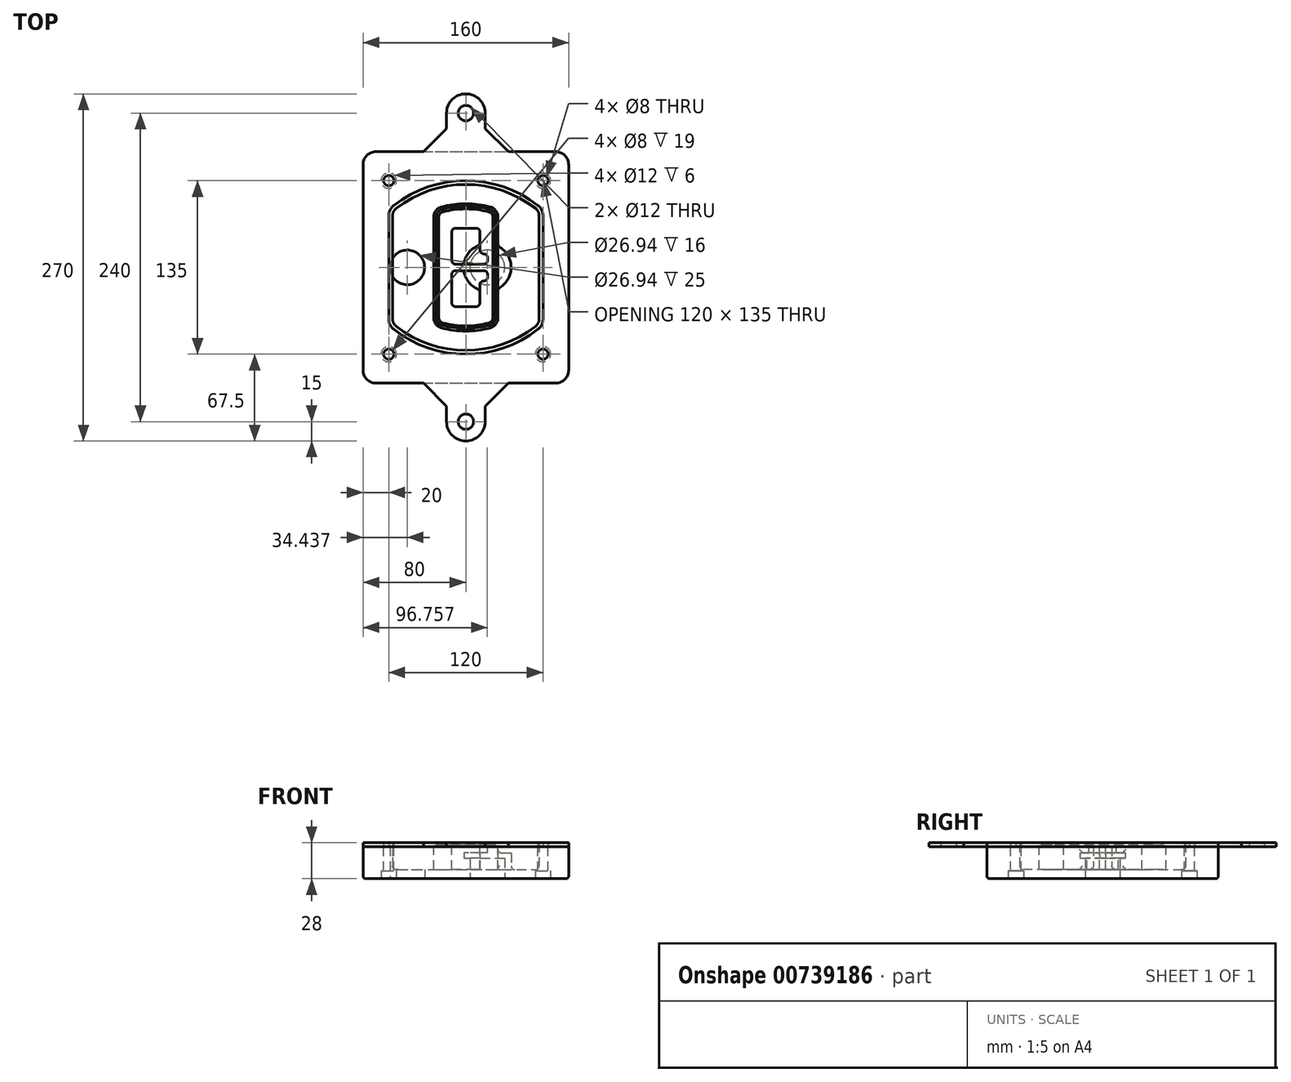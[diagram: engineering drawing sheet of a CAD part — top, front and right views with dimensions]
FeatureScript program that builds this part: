
annotation { "Feature Type Name" : "Feature", "Feature Type Description" : "" }
export const myFeature = defineFeature(function(context is Context, id is Id, definition is map)
    precondition{}
    {
        {
            var Q0;
            Q0=qCreatedBy(makeId("Top.planeOp"),FACE);
            var sketch = newSketch(context, id + "F0", { "sketchPlane" : qUnion([Q0])});
            skPoint(sketch, "E0.rect.middle", {"position": v(0, 0) * mm});
            skLineSegment(sketch, "E1.bottom", {"start": v(-70, -90) * mm, "end": v(70, -90) * mm});
            skLineSegment(sketch, "E1.top", {"start": v(-70, 90) * mm, "end": v(70, 90) * mm});
            skLineSegment(sketch, "E1.left", {"start": v(-80, -80) * mm, "end": v(-80, 80) * mm});
            skLineSegment(sketch, "E1.right", {"start": v(80, -80) * mm, "end": v(80, 80) * mm});
            skLineSegment(sketch, "E2", {"start": v(-80, 90) * mm, "end": v(80, -90) * mm, "construction": true});
            skLineSegment(sketch, "E3", {"start": v(80, 90) * mm, "end": v(-80, -90) * mm, "construction": true});
            skCircle(sketch, "E4", {"center": v(-60, 67.5) * mm, "radius": 4 * mm});
            skCircle(sketch, "E5", {"center": v(60, 67.5) * mm, "radius": 4 * mm});
            skCircle(sketch, "E6", {"center": v(60, -67.5) * mm, "radius": 4 * mm});
            skCircle(sketch, "E7", {"center": v(-60, -67.5) * mm, "radius": 4 * mm});
            skLineSegment(sketch, "E8", {"start": v(-60, 67.5) * mm, "end": v(60, 67.5) * mm, "construction": true});
            skLineSegment(sketch, "E9", {"start": v(60, 67.5) * mm, "end": v(60, -67.5) * mm, "construction": true});
            skLineSegment(sketch, "E10", {"start": v(60, -67.5) * mm, "end": v(-60, -67.5) * mm, "construction": true});
            skLineSegment(sketch, "E11", {"start": v(-60, -67.5) * mm, "end": v(-60, 67.5) * mm, "construction": true});
            skLineSegment(sketch, "E12", {"start": v(-60, 40.3) * mm, "end": v(-60, -40.3) * mm});
            skLineSegment(sketch, "E13", {"start": v(60, 40.3) * mm, "end": v(60, -40.3) * mm});
            skArc(sketch, "E14", {"start": v(56.15, 48.18) * mm, "mid": v(0, 67.5) * mm, "end": v(-56.15, 48.18) * mm});
            skArc(sketch, "E15", {"start": v(-56.15, -48.18) * mm, "mid": v(0, -67.5) * mm, "end": v(56.15, -48.18) * mm});
            skLineSegment(sketch, "E16", {"start": v(-60, 0) * mm, "end": v(60, 0) * mm, "construction": true});
            skPoint(sketch, "E17.visualSharp", {"position": v(-60, -45) * mm});
            skArc(sketch, "E17.filletArc", {"start": v(-60, -40.3) * mm, "mid": v(-58.99, -44.68) * mm, "end": v(-56.15, -48.18) * mm});
            skPoint(sketch, "E18.visualSharp", {"position": v(-60, 45) * mm});
            skArc(sketch, "E18.filletArc", {"start": v(-56.15, 48.18) * mm, "mid": v(-58.99, 44.68) * mm, "end": v(-60, 40.3) * mm});
            skPoint(sketch, "E19.visualSharp", {"position": v(60, 45) * mm});
            skArc(sketch, "E19.filletArc", {"start": v(60, 40.3) * mm, "mid": v(58.99, 44.68) * mm, "end": v(56.15, 48.18) * mm});
            skPoint(sketch, "E20.visualSharp", {"position": v(60, -45) * mm});
            skArc(sketch, "E20.filletArc", {"start": v(56.15, -48.18) * mm, "mid": v(58.99, -44.68) * mm, "end": v(60, -40.3) * mm});
            skPoint(sketch, "E21.visualSharp", {"position": v(-80, 90) * mm});
            skArc(sketch, "E21.filletArc", {"start": v(-70, 90) * mm, "mid": v(-77.07, 87.07) * mm, "end": v(-80, 80) * mm});
            skPoint(sketch, "E22.visualSharp", {"position": v(80, 90) * mm});
            skArc(sketch, "E22.filletArc", {"start": v(80, 80) * mm, "mid": v(77.07, 87.07) * mm, "end": v(70, 90) * mm});
            skPoint(sketch, "E23.visualSharp", {"position": v(80, -90) * mm});
            skArc(sketch, "E23.filletArc", {"start": v(70, -90) * mm, "mid": v(77.07, -87.07) * mm, "end": v(80, -80) * mm});
            skPoint(sketch, "E24.visualSharp", {"position": v(-80, -90) * mm});
            skArc(sketch, "E24.filletArc", {"start": v(-80, -80) * mm, "mid": v(-77.07, -87.07) * mm, "end": v(-70, -90) * mm});
            skArc(sketch, "E25.0", {"start": v(57, 40.3) * mm, "mid": v(56.3, 43.36) * mm, "end": v(54.3, 45.81) * mm});
            skLineSegment(sketch, "E25.1", {"start": v(57, 40.3) * mm, "end": v(57, -40.3) * mm});
            skArc(sketch, "E25.2", {"start": v(54.3, -45.81) * mm, "mid": v(56.3, -43.36) * mm, "end": v(57, -40.3) * mm});
            skArc(sketch, "E25.3", {"start": v(-54.3, -45.81) * mm, "mid": v(0, -64.5) * mm, "end": v(54.3, -45.81) * mm});
            skArc(sketch, "E25.4", {"start": v(-57, -40.3) * mm, "mid": v(-56.3, -43.36) * mm, "end": v(-54.3, -45.81) * mm});
            skArc(sketch, "E25.5", {"start": v(54.3, 45.81) * mm, "mid": v(0, 64.5) * mm, "end": v(-54.3, 45.81) * mm});
            skLineSegment(sketch, "E25.6", {"start": v(-57, 40.3) * mm, "end": v(-57, -40.3) * mm});
            skArc(sketch, "E25.7", {"start": v(-54.3, 45.81) * mm, "mid": v(-56.3, 43.36) * mm, "end": v(-57, 40.3) * mm});
            skArc(sketch, "E26.0", {"start": v(-58.62, 51.33) * mm, "mid": v(-62.58, 46.43) * mm, "end": v(-64, 40.3) * mm});
            skArc(sketch, "E26.1", {"start": v(58.62, 51.33) * mm, "mid": v(0, 71.5) * mm, "end": v(-58.62, 51.33) * mm});
            skArc(sketch, "E26.2", {"start": v(64, 40.3) * mm, "mid": v(62.58, 46.43) * mm, "end": v(58.62, 51.33) * mm});
            skLineSegment(sketch, "E26.3", {"start": v(64, 40.3) * mm, "end": v(64, -40.3) * mm});
            skArc(sketch, "E26.4", {"start": v(58.62, -51.33) * mm, "mid": v(62.58, -46.43) * mm, "end": v(64, -40.3) * mm});
            skLineSegment(sketch, "E26.5", {"start": v(-64, 40.3) * mm, "end": v(-64, -40.3) * mm});
            skArc(sketch, "E26.6", {"start": v(-58.62, -51.33) * mm, "mid": v(0, -71.5) * mm, "end": v(58.62, -51.33) * mm});
            skArc(sketch, "E26.7", {"start": v(-64, -40.3) * mm, "mid": v(-62.58, -46.43) * mm, "end": v(-58.62, -51.33) * mm});
            skSolve(sketch);
        }
        {
            var Q0;
            Q0=makeQuery(id+"F0.imprint","IMPRINT",FACE,{"disambiguationData":[TD([[makeQuery(id+"F0.imprint","IMPRINT",EDGE,{"derivedFrom":sQuery(id+"F0.wireOp",EDGE,"E1.bottom")}),1.0]])]});
            var Q1;
            Q1=makeQuery(id+"F0.imprint","IMPRINT",FACE,{"disambiguationData":[TD([[makeQuery(id+"F0.imprint","IMPRINT",EDGE,{"derivedFrom":sQuery(id+"F0.wireOp",EDGE,"E12")}),1.0]])]});
            var Q2;
            Q2=makeQuery(id+"F0.imprint","IMPRINT",FACE,{"disambiguationData":[TD([[makeQuery(id+"F0.imprint","IMPRINT",EDGE,{"derivedFrom":sQuery(id+"F0.wireOp",EDGE,"E25.0")}),1.0]])]});
            var Q3;
            Q3=makeQuery(id+"F0.imprint","IMPRINT",FACE,{"disambiguationData":[TD([[makeQuery(id+"F0.imprint","IMPRINT",EDGE,{"derivedFrom":sQuery(id+"F0.wireOp",EDGE,"E12")}),-1.0]])]});
            extrude(context, id + "F1", {"entities" : qUnion([Q0, Q1, Q2, Q3]), "oppositeDirection" : true, "depth" : 25 * mm});
        }
        {
            var Q0;
            Q0=makeQuery(id+"F0.imprint","IMPRINT",FACE,{"disambiguationData":[TD([[makeQuery(id+"F0.imprint","IMPRINT",EDGE,{"derivedFrom":sQuery(id+"F0.wireOp",EDGE,"E12")}),1.0]])]});
            extrude(context, id + "F2", {"entities" : qUnion([Q0]), "operationType" : NewBodyOperationType.ADD, "depth" : 3 * mm});
        }
        {
            var Q0;
            Q0=makeQuery(id+"F0.imprint","IMPRINT",FACE,{"disambiguationData":[TD([[makeQuery(id+"F0.imprint","IMPRINT",EDGE,{"derivedFrom":sQuery(id+"F0.wireOp",EDGE,"E25.0")}),1.0]])]});
            extrude(context, id + "F3", {"entities" : qUnion([Q0]), "operationType" : NewBodyOperationType.REMOVE, "oppositeDirection" : true, "depth" : 18 * mm});
        }
        {
            var Q0;
            Q0=makeQuery(id+"F2.opExtrude","CAP_FACE",FACE,{"disambiguationData":[OSD([sQuery(id+"F0.wireOp",EDGE,"E12"),sQuery(id+"F0.wireOp",EDGE,"E13"),sQuery(id+"F0.wireOp",EDGE,"E14"),sQuery(id+"F0.wireOp",EDGE,"E15"),sQuery(id+"F0.wireOp",EDGE,"E17.filletArc"),sQuery(id+"F0.wireOp",EDGE,"E18.filletArc"),sQuery(id+"F0.wireOp",EDGE,"E19.filletArc"),sQuery(id+"F0.wireOp",EDGE,"E20.filletArc"),sQuery(id+"F0.wireOp",EDGE,"E25.0"),sQuery(id+"F0.wireOp",EDGE,"E25.1"),sQuery(id+"F0.wireOp",EDGE,"E25.2"),sQuery(id+"F0.wireOp",EDGE,"E25.3"),sQuery(id+"F0.wireOp",EDGE,"E25.4"),sQuery(id+"F0.wireOp",EDGE,"E25.5"),sQuery(id+"F0.wireOp",EDGE,"E25.6"),sQuery(id+"F0.wireOp",EDGE,"E25.7")])],"isStart":false});
            var sketch = newSketch(context, id + "F4", { "sketchPlane" : qUnion([Q0])});
            skArc(sketch, "E27.0", {"start": v(-19.08, -46.97) * mm, "mid": v(0, -49.5) * mm, "end": v(19.08, -46.97) * mm});
            skArc(sketch, "E28.0", {"start": v(19.08, 46.97) * mm, "mid": v(0, 49.5) * mm, "end": v(-19.08, 46.97) * mm});
            skLineSegment(sketch, "E29", {"start": v(-25, 39.25) * mm, "end": v(-25, -39.25) * mm});
            skLineSegment(sketch, "E30", {"start": v(25, 39.25) * mm, "end": v(25, -39.25) * mm});
            skLineSegment(sketch, "E31", {"start": v(-25, 45.1) * mm, "end": v(25, 45.1) * mm, "construction": true});
            skLineSegment(sketch, "E32", {"start": v(-25, -45.1) * mm, "end": v(25, -45.1) * mm, "construction": true});
            skPoint(sketch, "E33.visualSharp", {"position": v(-25, 45.1) * mm});
            skArc(sketch, "E33.filletArc", {"start": v(-19.08, 46.97) * mm, "mid": v(-23.35, 44.11) * mm, "end": v(-25, 39.25) * mm});
            skPoint(sketch, "E34.visualSharp", {"position": v(25, 45.1) * mm});
            skArc(sketch, "E34.filletArc", {"start": v(25, 39.25) * mm, "mid": v(23.35, 44.11) * mm, "end": v(19.08, 46.97) * mm});
            skPoint(sketch, "E35.visualSharp", {"position": v(25, -45.1) * mm});
            skArc(sketch, "E35.filletArc", {"start": v(19.08, -46.97) * mm, "mid": v(23.35, -44.11) * mm, "end": v(25, -39.25) * mm});
            skPoint(sketch, "E36.visualSharp", {"position": v(-25, -45.1) * mm});
            skArc(sketch, "E36.filletArc", {"start": v(-25, -39.25) * mm, "mid": v(-23.35, -44.11) * mm, "end": v(-19.08, -46.97) * mm});
            skArc(sketch, "E37.0", {"start": v(54.3, 45.81) * mm, "mid": v(0, 64.5) * mm, "end": v(-54.3, 45.81) * mm});
            skArc(sketch, "E37.1", {"start": v(-54.3, 45.81) * mm, "mid": v(-56.3, 43.36) * mm, "end": v(-57, 40.3) * mm});
            skLineSegment(sketch, "E37.2", {"start": v(-57, 40.3) * mm, "end": v(-57, -40.3) * mm});
            skArc(sketch, "E37.3", {"start": v(-57, -40.3) * mm, "mid": v(-56.3, -43.36) * mm, "end": v(-54.3, -45.81) * mm});
            skArc(sketch, "E37.4", {"start": v(-54.3, -45.81) * mm, "mid": v(0, -64.5) * mm, "end": v(54.3, -45.81) * mm});
            skArc(sketch, "E37.5", {"start": v(54.3, -45.81) * mm, "mid": v(56.3, -43.36) * mm, "end": v(57, -40.3) * mm});
            skLineSegment(sketch, "E37.6", {"start": v(57, 40.3) * mm, "end": v(57, -40.3) * mm});
            skArc(sketch, "E37.7", {"start": v(57, 40.3) * mm, "mid": v(56.3, 43.36) * mm, "end": v(54.3, 45.81) * mm});
            skLineSegment(sketch, "E38.0", {"start": v(23, 39.25) * mm, "end": v(23, -39.25) * mm});
            skArc(sketch, "E38.1", {"start": v(18.56, -45.04) * mm, "mid": v(21.76, -42.9) * mm, "end": v(23, -39.25) * mm});
            skArc(sketch, "E38.2", {"start": v(-18.56, -45.04) * mm, "mid": v(0, -47.5) * mm, "end": v(18.56, -45.04) * mm});
            skArc(sketch, "E38.3", {"start": v(-23, -39.25) * mm, "mid": v(-21.76, -42.9) * mm, "end": v(-18.56, -45.04) * mm});
            skLineSegment(sketch, "E38.4", {"start": v(-23, 39.25) * mm, "end": v(-23, -39.25) * mm});
            skArc(sketch, "E38.5", {"start": v(23, 39.25) * mm, "mid": v(21.76, 42.9) * mm, "end": v(18.56, 45.04) * mm});
            skArc(sketch, "E38.6", {"start": v(-18.56, 45.04) * mm, "mid": v(-21.76, 42.9) * mm, "end": v(-23, 39.25) * mm});
            skArc(sketch, "E38.7", {"start": v(18.56, 45.04) * mm, "mid": v(0, 47.5) * mm, "end": v(-18.56, 45.04) * mm});
            skArc(sketch, "E39.0", {"start": v(21, 39.25) * mm, "mid": v(20.18, 41.68) * mm, "end": v(18.04, 43.1) * mm});
            skLineSegment(sketch, "E39.1", {"start": v(21, 39.25) * mm, "end": v(21, -39.25) * mm});
            skArc(sketch, "E39.2", {"start": v(18.04, -43.1) * mm, "mid": v(20.18, -41.68) * mm, "end": v(21, -39.25) * mm});
            skArc(sketch, "E39.3", {"start": v(-18.04, -43.1) * mm, "mid": v(0, -45.5) * mm, "end": v(18.04, -43.1) * mm});
            skArc(sketch, "E39.4", {"start": v(-21, -39.25) * mm, "mid": v(-20.18, -41.68) * mm, "end": v(-18.04, -43.1) * mm});
            skArc(sketch, "E39.5", {"start": v(18.04, 43.1) * mm, "mid": v(0, 45.5) * mm, "end": v(-18.04, 43.1) * mm});
            skLineSegment(sketch, "E39.6", {"start": v(-21, 39.25) * mm, "end": v(-21, -39.25) * mm});
            skArc(sketch, "E39.7", {"start": v(-18.04, 43.1) * mm, "mid": v(-20.18, 41.68) * mm, "end": v(-21, 39.25) * mm});
            skLineSegment(sketch, "E40", {"start": v(-25, 0) * mm, "end": v(25, 0) * mm, "construction": true});
            skLineSegment(sketch, "E41", {"start": v(-11, 5.5) * mm, "end": v(-11, 27.5) * mm});
            skLineSegment(sketch, "E42", {"start": v(-8, 30.5) * mm, "end": v(8, 30.5) * mm});
            skLineSegment(sketch, "E43", {"start": v(11, 27.5) * mm, "end": v(11, 13.5) * mm});
            skLineSegment(sketch, "E44", {"start": v(14, 10.5) * mm, "end": v(14, 10.5) * mm});
            skLineSegment(sketch, "E45", {"start": v(17, 7.5) * mm, "end": v(17, 5.5) * mm});
            skLineSegment(sketch, "E46", {"start": v(14, 2.5) * mm, "end": v(-8, 2.5) * mm});
            skPoint(sketch, "E47.visualSharp", {"position": v(-11, 30.5) * mm});
            skArc(sketch, "E47.filletArc", {"start": v(-8, 30.5) * mm, "mid": v(-10.12, 29.62) * mm, "end": v(-11, 27.5) * mm});
            skPoint(sketch, "E48.visualSharp", {"position": v(11, 30.5) * mm});
            skArc(sketch, "E48.filletArc", {"start": v(11, 27.5) * mm, "mid": v(10.12, 29.62) * mm, "end": v(8, 30.5) * mm});
            skPoint(sketch, "E49.visualSharp", {"position": v(11, 10.5) * mm});
            skArc(sketch, "E49.filletArc", {"start": v(11, 13.5) * mm, "mid": v(11.88, 11.38) * mm, "end": v(14, 10.5) * mm});
            skPoint(sketch, "E50.visualSharp", {"position": v(17, 10.5) * mm});
            skArc(sketch, "E50.filletArc", {"start": v(17, 7.5) * mm, "mid": v(16.12, 9.62) * mm, "end": v(14, 10.5) * mm});
            skPoint(sketch, "E51.visualSharp", {"position": v(17, 2.5) * mm});
            skArc(sketch, "E51.filletArc", {"start": v(14, 2.5) * mm, "mid": v(16.12, 3.38) * mm, "end": v(17, 5.5) * mm});
            skPoint(sketch, "E52.visualSharp", {"position": v(-11, 2.5) * mm});
            skArc(sketch, "E52.filletArc", {"start": v(-11, 5.5) * mm, "mid": v(-10.12, 3.38) * mm, "end": v(-8, 2.5) * mm});
            skLineSegment(sketch, "E53.0.MirrorCS", {"start": v(14, -2.5) * mm, "end": v(-8, -2.5) * mm});
            skArc(sketch, "E54.0.MirrorCS", {"start": v(-11, -5.5) * mm, "mid": v(-10.12, -3.38) * mm, "end": v(-8, -2.5) * mm});
            skLineSegment(sketch, "E55.0.MirrorCS", {"start": v(-11, -5.5) * mm, "end": v(-11, -27.5) * mm});
            skArc(sketch, "E56.0.MirrorCS", {"start": v(-8, -30.5) * mm, "mid": v(-10.12, -29.62) * mm, "end": v(-11, -27.5) * mm});
            skLineSegment(sketch, "E57.0.MirrorCS", {"start": v(-8, -30.5) * mm, "end": v(8, -30.5) * mm});
            skArc(sketch, "E58.0.MirrorCS", {"start": v(11, -27.5) * mm, "mid": v(10.12, -29.62) * mm, "end": v(8, -30.5) * mm});
            skLineSegment(sketch, "E59.0.MirrorCS", {"start": v(11, -27.5) * mm, "end": v(11, -13.5) * mm});
            skArc(sketch, "E60.0.MirrorCS", {"start": v(11, -13.5) * mm, "mid": v(11.88, -11.38) * mm, "end": v(14, -10.5) * mm});
            skArc(sketch, "E61.0.MirrorCS", {"start": v(17, -7.5) * mm, "mid": v(16.12, -9.62) * mm, "end": v(14, -10.5) * mm});
            skLineSegment(sketch, "E62.0.MirrorCS", {"start": v(17, -7.5) * mm, "end": v(17, -5.5) * mm});
            skArc(sketch, "E63.0.MirrorCS", {"start": v(14, -2.5) * mm, "mid": v(16.12, -3.38) * mm, "end": v(17, -5.5) * mm});
            skSolve(sketch);
        }
        {
            var Q0;
            Q0=makeQuery(id+"F4.imprint","IMPRINT",FACE,{"disambiguationData":[TD([[makeQuery(id+"F4.imprint","IMPRINT",EDGE,{"derivedFrom":sQuery(id+"F4.wireOp",EDGE,"E27.0")}),1.0]])]});
            var Q1;
            Q1=makeQuery(id+"F4.imprint","IMPRINT",FACE,{"disambiguationData":[TD([[makeQuery(id+"F4.imprint","IMPRINT",EDGE,{"derivedFrom":sQuery(id+"F4.wireOp",EDGE,"E38.0")}),-1.0]])]});
            var Q2;
            Q2=makeQuery(id+"F4.imprint","IMPRINT",FACE,{"disambiguationData":[TD([[makeQuery(id+"F4.imprint","IMPRINT",EDGE,{"derivedFrom":sQuery(id+"F4.wireOp",EDGE,"E39.0")}),1.0]])]});
            extrude(context, id + "F5", {"entities" : qUnion([Q0, Q1, Q2]), "operationType" : NewBodyOperationType.ADD, "endBound" : BoundingType.UP_TO_NEXT, "oppositeDirection" : true, "depth" : 25 * mm});
        }
        {
            var Q0;
            Q0=makeQuery(id+"F4.imprint","IMPRINT",FACE,{"disambiguationData":[TD([[makeQuery(id+"F4.imprint","IMPRINT",EDGE,{"derivedFrom":sQuery(id+"F4.wireOp",EDGE,"E38.0")}),-1.0]])]});
            extrude(context, id + "F6", {"entities" : qUnion([Q0]), "operationType" : NewBodyOperationType.REMOVE, "oppositeDirection" : true, "depth" : 2 * mm});
        }
        {
            var Q0;
            Q0=makeQuery(id+"F1.opExtrude","CAP_FACE",FACE,{"disambiguationData":[OSD([sQuery(id+"F0.wireOp",EDGE,"E1.bottom"),sQuery(id+"F0.wireOp",EDGE,"E1.top"),sQuery(id+"F0.wireOp",EDGE,"E1.left"),sQuery(id+"F0.wireOp",EDGE,"E1.right"),sQuery(id+"F0.wireOp",EDGE,"E4"),sQuery(id+"F0.wireOp",EDGE,"E5"),sQuery(id+"F0.wireOp",EDGE,"E6"),sQuery(id+"F0.wireOp",EDGE,"E7"),sQuery(id+"F0.wireOp",EDGE,"E21.filletArc"),sQuery(id+"F0.wireOp",EDGE,"E22.filletArc"),sQuery(id+"F0.wireOp",EDGE,"E23.filletArc"),sQuery(id+"F0.wireOp",EDGE,"E24.filletArc")])],"isStart":false});
            var sketch = newSketch(context, id + "F7", { "sketchPlane" : qUnion([Q0])});
            skCircle(sketch, "E64", {"center": v(16.76, 0) * mm, "radius": 13.47 * mm});
            skCircle(sketch, "E65", {"center": v(-45.56, 0) * mm, "radius": 13.47 * mm});
            skLineSegment(sketch, "E66", {"start": v(80, 0) * mm, "end": v(-80, 0) * mm});
            skCircle(sketch, "E67", {"center": v(16.76, 0) * mm, "radius": 18.47 * mm});
            skCircle(sketch, "E68", {"center": v(60, -67.5) * mm, "radius": 6 * mm});
            skCircle(sketch, "E69", {"center": v(-60, -67.5) * mm, "radius": 6 * mm});
            skCircle(sketch, "E70", {"center": v(-60, 67.5) * mm, "radius": 6 * mm});
            skCircle(sketch, "E71", {"center": v(60, 67.5) * mm, "radius": 6 * mm});
            skSolve(sketch);
        }
        {
            var Q0;
            {var subQ1=sQuery(id+"F7.wireOp",EDGE,"E66");var subQ4=sQuery(id+"F7.wireOp",EDGE,"E64");var subQ6=makeQuery(id+"F7.imprint","INTERSECT",VERTEX,{"disambiguationData":[OD(0.0)],"derivedFrom":[subQ4,subQ1]});Q0=makeQuery(id+"F7.imprint","IMPRINT",FACE,{"disambiguationData":[TD([[makeQuery(id+"F7.imprint","IMPRINT",EDGE,{"disambiguationData":[TD([[subQ6,-1.0]])],"derivedFrom":subQ4}),-1.0]])]});}
            var Q1;
            {var subQ0=sQuery(id+"F7.wireOp",EDGE,"E66");var subQ1=sQuery(id+"F7.wireOp",EDGE,"E64");var subQ3=makeQuery(id+"F7.imprint","INTERSECT",VERTEX,{"disambiguationData":[OD(0.0)],"derivedFrom":[subQ1,subQ0]});Q1=makeQuery(id+"F7.imprint","IMPRINT",FACE,{"disambiguationData":[TD([[makeQuery(id+"F7.imprint","IMPRINT",EDGE,{"disambiguationData":[TD([[subQ3,-1.0]])],"derivedFrom":subQ1}),1.0]])]});}
            var Q2;
            {var subQ0=sQuery(id+"F7.wireOp",EDGE,"E66");var subQ1=sQuery(id+"F7.wireOp",EDGE,"E64");var subQ3=makeQuery(id+"F7.imprint","INTERSECT",VERTEX,{"disambiguationData":[OD(0.0)],"derivedFrom":[subQ1,subQ0]});Q2=makeQuery(id+"F7.imprint","IMPRINT",FACE,{"disambiguationData":[TD([[makeQuery(id+"F7.imprint","IMPRINT",EDGE,{"disambiguationData":[TD([[subQ3,1.0]])],"derivedFrom":subQ1}),1.0]])]});}
            var Q3;
            {var subQ1=sQuery(id+"F7.wireOp",EDGE,"E66");var subQ4=sQuery(id+"F7.wireOp",EDGE,"E64");var subQ6=makeQuery(id+"F7.imprint","INTERSECT",VERTEX,{"disambiguationData":[OD(0.0)],"derivedFrom":[subQ4,subQ1]});Q3=makeQuery(id+"F7.imprint","IMPRINT",FACE,{"disambiguationData":[TD([[makeQuery(id+"F7.imprint","IMPRINT",EDGE,{"disambiguationData":[TD([[subQ6,1.0]])],"derivedFrom":subQ4}),-1.0]])]});}
            extrude(context, id + "F8", {"entities" : qUnion([Q0, Q1, Q2, Q3]), "operationType" : NewBodyOperationType.ADD, "oppositeDirection" : true, "depth" : 20 * mm});
        }
        {
            var Q0;
            {var subQ0=sQuery(id+"F7.wireOp",EDGE,"E66");var subQ1=sQuery(id+"F7.wireOp",EDGE,"E64");var subQ3=makeQuery(id+"F7.imprint","INTERSECT",VERTEX,{"disambiguationData":[OD(0.0)],"derivedFrom":[subQ1,subQ0]});Q0=makeQuery(id+"F7.imprint","IMPRINT",FACE,{"disambiguationData":[TD([[makeQuery(id+"F7.imprint","IMPRINT",EDGE,{"disambiguationData":[TD([[subQ3,-1.0]])],"derivedFrom":subQ1}),1.0]])]});}
            var Q1;
            {var subQ0=sQuery(id+"F7.wireOp",EDGE,"E66");var subQ1=sQuery(id+"F7.wireOp",EDGE,"E64");var subQ3=makeQuery(id+"F7.imprint","INTERSECT",VERTEX,{"disambiguationData":[OD(0.0)],"derivedFrom":[subQ1,subQ0]});Q1=makeQuery(id+"F7.imprint","IMPRINT",FACE,{"disambiguationData":[TD([[makeQuery(id+"F7.imprint","IMPRINT",EDGE,{"disambiguationData":[TD([[subQ3,1.0]])],"derivedFrom":subQ1}),1.0]])]});}
            extrude(context, id + "F9", {"entities" : qUnion([Q0, Q1]), "operationType" : NewBodyOperationType.REMOVE, "oppositeDirection" : true, "depth" : 16 * mm});
        }
        {
            var Q0;
            {var subQ0=sQuery(id+"F7.wireOp",EDGE,"E66");var subQ1=sQuery(id+"F7.wireOp",EDGE,"E65");var subQ3=makeQuery(id+"F7.imprint","INTERSECT",VERTEX,{"disambiguationData":[OD(0.0)],"derivedFrom":[subQ1,subQ0]});Q0=makeQuery(id+"F7.imprint","IMPRINT",FACE,{"disambiguationData":[TD([[makeQuery(id+"F7.imprint","IMPRINT",EDGE,{"disambiguationData":[TD([[subQ3,-1.0]])],"derivedFrom":subQ1}),1.0]])]});}
            var Q1;
            {var subQ0=sQuery(id+"F7.wireOp",EDGE,"E66");var subQ1=sQuery(id+"F7.wireOp",EDGE,"E65");var subQ3=makeQuery(id+"F7.imprint","INTERSECT",VERTEX,{"disambiguationData":[OD(0.0)],"derivedFrom":[subQ1,subQ0]});Q1=makeQuery(id+"F7.imprint","IMPRINT",FACE,{"disambiguationData":[TD([[makeQuery(id+"F7.imprint","IMPRINT",EDGE,{"disambiguationData":[TD([[subQ3,1.0]])],"derivedFrom":subQ1}),1.0]])]});}
            extrude(context, id + "F10", {"entities" : qUnion([Q0, Q1]), "operationType" : NewBodyOperationType.REMOVE, "oppositeDirection" : true, "depth" : 25 * mm});
        }
        {
            var Q0;
            Q0=makeQuery(id+"F7.imprint","IMPRINT",FACE,{"disambiguationData":[TD([[makeQuery(id+"F7.imprint","IMPRINT",EDGE,{"derivedFrom":sQuery(id+"F7.wireOp",EDGE,"E68")}),1.0]])]});
            var Q1;
            Q1=makeQuery(id+"F7.imprint","IMPRINT",FACE,{"disambiguationData":[TD([[makeQuery(id+"F7.imprint","IMPRINT",EDGE,{"derivedFrom":makeQuery(id+"F1.opExtrude","CAP_EDGE",EDGE,{"disambiguationData":[OSD([sQuery(id+"F0.wireOp",EDGE,"E5")])],"isStart":false})}),-1.0]])]});
            var Q2;
            Q2=makeQuery(id+"F7.imprint","IMPRINT",FACE,{"disambiguationData":[TD([[makeQuery(id+"F7.imprint","IMPRINT",EDGE,{"derivedFrom":sQuery(id+"F7.wireOp",EDGE,"E69")}),1.0]])]});
            var Q3;
            Q3=makeQuery(id+"F7.imprint","IMPRINT",FACE,{"disambiguationData":[TD([[makeQuery(id+"F7.imprint","IMPRINT",EDGE,{"derivedFrom":makeQuery(id+"F1.opExtrude","CAP_EDGE",EDGE,{"disambiguationData":[OSD([sQuery(id+"F0.wireOp",EDGE,"E4")])],"isStart":false})}),-1.0]])]});
            var Q4;
            Q4=makeQuery(id+"F7.imprint","IMPRINT",FACE,{"disambiguationData":[TD([[makeQuery(id+"F7.imprint","IMPRINT",EDGE,{"derivedFrom":sQuery(id+"F7.wireOp",EDGE,"E70")}),1.0]])]});
            var Q5;
            Q5=makeQuery(id+"F7.imprint","IMPRINT",FACE,{"disambiguationData":[TD([[makeQuery(id+"F7.imprint","IMPRINT",EDGE,{"derivedFrom":makeQuery(id+"F1.opExtrude","CAP_EDGE",EDGE,{"disambiguationData":[OSD([sQuery(id+"F0.wireOp",EDGE,"E7")])],"isStart":false})}),-1.0]])]});
            var Q6;
            Q6=makeQuery(id+"F7.imprint","IMPRINT",FACE,{"disambiguationData":[TD([[makeQuery(id+"F7.imprint","IMPRINT",EDGE,{"derivedFrom":sQuery(id+"F7.wireOp",EDGE,"E71")}),1.0]])]});
            var Q7;
            Q7=makeQuery(id+"F7.imprint","IMPRINT",FACE,{"disambiguationData":[TD([[makeQuery(id+"F7.imprint","IMPRINT",EDGE,{"derivedFrom":makeQuery(id+"F1.opExtrude","CAP_EDGE",EDGE,{"disambiguationData":[OSD([sQuery(id+"F0.wireOp",EDGE,"E6")])],"isStart":false})}),-1.0]])]});
            extrude(context, id + "F11", {"entities" : qUnion([Q0, Q1, Q2, Q3, Q4, Q5, Q6, Q7]), "operationType" : NewBodyOperationType.REMOVE, "oppositeDirection" : true, "depth" : 6 * mm});
        }
        {
            var Q0;
            Q0=makeQuery(id+"F9.boolean.opBoolean","COPY",FACE,{"derivedFrom":makeQuery(id+"F9.opExtrude","CAP_FACE",FACE,{"disambiguationData":[OSD([sQuery(id+"F7.wireOp",EDGE,"E64")])],"isStart":false})});
            var sketch = newSketch(context, id + "F12", { "sketchPlane" : qUnion([Q0])});
            skArc(sketch, "E72.0", {"start": v(11, 17.55) * mm, "mid": v(2.57, 11.82) * mm, "end": v(-1.54, 2.5) * mm});
            skArc(sketch, "E72.1", {"start": v(-1.54, -2.5) * mm, "mid": v(2.57, -11.82) * mm, "end": v(11, -17.55) * mm});
            skLineSegment(sketch, "E73", {"start": v(-1.54, -2.5) * mm, "end": v(14, -2.5) * mm});
            skLineSegment(sketch, "E74.0", {"start": v(14, 2.5) * mm, "end": v(-1.54, 2.5) * mm});
            skArc(sketch, "E74.1", {"start": v(14, 2.5) * mm, "mid": v(16.12, 3.38) * mm, "end": v(17, 5.5) * mm});
            skLineSegment(sketch, "E74.2", {"start": v(17, 7.5) * mm, "end": v(17, 5.5) * mm});
            skArc(sketch, "E74.3", {"start": v(17, 7.5) * mm, "mid": v(16.12, 9.62) * mm, "end": v(14, 10.5) * mm});
            skArc(sketch, "E74.4", {"start": v(11, 13.5) * mm, "mid": v(11.88, 11.38) * mm, "end": v(14, 10.5) * mm});
            skLineSegment(sketch, "E74.5", {"start": v(11, 17.55) * mm, "end": v(11, 13.5) * mm});
            skLineSegment(sketch, "E74.7", {"start": v(14, -2.5) * mm, "end": v(-1.54, -2.5) * mm});
            skArc(sketch, "E74.8", {"start": v(14, -2.5) * mm, "mid": v(16.12, -3.38) * mm, "end": v(17, -5.5) * mm});
            skLineSegment(sketch, "E74.9", {"start": v(17, -7.5) * mm, "end": v(17, -5.5) * mm});
            skArc(sketch, "E74.10", {"start": v(17, -7.5) * mm, "mid": v(16.12, -9.62) * mm, "end": v(14, -10.5) * mm});
            skArc(sketch, "E74.11", {"start": v(11, -13.5) * mm, "mid": v(11.88, -11.38) * mm, "end": v(14, -10.5) * mm});
            skLineSegment(sketch, "E74.12", {"start": v(11, -17.55) * mm, "end": v(11, -13.5) * mm});
            skPoint(sketch, "E75.orphan", {"position": v(11, -27.5) * mm});
            skPoint(sketch, "E76.orphan", {"position": v(-8, -2.5) * mm});
            skPoint(sketch, "E77.orphan", {"position": v(-8, 2.5) * mm});
            skPoint(sketch, "E78.orphan", {"position": v(11, 27.5) * mm});
            skSolve(sketch);
        }
        {
            var Q0;
            {var subQ7=sQuery(id+"F12.wireOp",EDGE,"E72.0");var subQ14=sQuery(id+"F12.wireOp",EDGE,"E72.1");var subQ16=sQuery(id+"F12.wireOp",EDGE,"E74.1");var subQ18=sQuery(id+"F12.wireOp",EDGE,"E74.8");Q0=qUnion([makeQuery(id+"F12.imprint","IMPRINT",FACE,{"disambiguationData":[TD([[makeQuery(id+"F12.imprint","IMPRINT",EDGE,{"derivedFrom":subQ7}),1.0]])]}),makeQuery(id+"F12.imprint","IMPRINT",FACE,{"disambiguationData":[TD([[makeQuery(id+"F12.imprint","IMPRINT",EDGE,{"derivedFrom":subQ14}),1.0]])]}),makeQuery(id+"F12.imprint","IMPRINT",FACE,{"disambiguationData":[TD([[makeQuery(id+"F12.imprint","IMPRINT",EDGE,{"derivedFrom":subQ16}),1.0]])]}),makeQuery(id+"F12.imprint","IMPRINT",FACE,{"disambiguationData":[TD([[makeQuery(id+"F12.imprint","IMPRINT",EDGE,{"derivedFrom":subQ18}),-1.0]])]})]);}
            var Q1;
            Q1=makeQuery(id+"F5.boolean.opBoolean","SPLIT",FACE,{"disambiguationData":[TD([makeQuery(id+"F5.opExtrude","SWEPT_FACE",FACE,{"disambiguationData":[OSD([sQuery(id+"F4.wireOp",EDGE,"E41")])]})])],"derivedFrom":makeQuery(id+"F3.boolean.opBoolean","COPY",FACE,{"derivedFrom":makeQuery(id+"F3.opExtrude","CAP_FACE",FACE,{"disambiguationData":[OSD([sQuery(id+"F0.wireOp",EDGE,"E25.0"),sQuery(id+"F0.wireOp",EDGE,"E25.1"),sQuery(id+"F0.wireOp",EDGE,"E25.2"),sQuery(id+"F0.wireOp",EDGE,"E25.3"),sQuery(id+"F0.wireOp",EDGE,"E25.4"),sQuery(id+"F0.wireOp",EDGE,"E25.5"),sQuery(id+"F0.wireOp",EDGE,"E25.6"),sQuery(id+"F0.wireOp",EDGE,"E25.7")])],"isStart":false})})});
            extrude(context, id + "F13", {"entities" : qUnion([Q0]), "operationType" : NewBodyOperationType.REMOVE, "endBound" : BoundingType.UP_TO_SURFACE, "endBoundEntityFace" : qUnion([Q1]), "depth" : 25 * mm});
        }
        {
            var Q0;
            Q0=makeQuery(id+"F3.boolean.opBoolean","COPY",EDGE,{"derivedFrom":makeQuery(id+"F3.opExtrude","CAP_EDGE",EDGE,{"disambiguationData":[OSD([sQuery(id+"F0.wireOp",EDGE,"E25.6")])],"isStart":false})});
            var Q1;
            Q1=makeQuery(id+"F8.boolean.opBoolean","INTERSECT",EDGE,{"derivedFrom":[makeQuery(id+"F5.opExtrude","SWEPT_FACE",FACE,{"disambiguationData":[OSD([sQuery(id+"F4.wireOp",EDGE,"E30")])]}),makeQuery(id+"F8.opExtrude","CAP_FACE",FACE,{"disambiguationData":[OSD([sQuery(id+"F7.wireOp",EDGE,"E67")])],"isStart":false})]});
            var Q2;
            Q2=makeQuery(id+"F8.boolean.opBoolean","INTERSECT",EDGE,{"disambiguationData":[OD(1.0)],"derivedFrom":[makeQuery(id+"F5.opExtrude","SWEPT_FACE",FACE,{"disambiguationData":[OSD([sQuery(id+"F4.wireOp",EDGE,"E30")])]}),makeQuery(id+"F8.opExtrude","SWEPT_FACE",FACE,{"disambiguationData":[OSD([sQuery(id+"F7.wireOp",EDGE,"E67")])]})]});
            var Q3;
            {var subQ0=makeQuery(id+"F3.boolean.opBoolean","COPY",FACE,{"derivedFrom":makeQuery(id+"F3.opExtrude","CAP_FACE",FACE,{"disambiguationData":[OSD([sQuery(id+"F0.wireOp",EDGE,"E25.0"),sQuery(id+"F0.wireOp",EDGE,"E25.1"),sQuery(id+"F0.wireOp",EDGE,"E25.2"),sQuery(id+"F0.wireOp",EDGE,"E25.3"),sQuery(id+"F0.wireOp",EDGE,"E25.4"),sQuery(id+"F0.wireOp",EDGE,"E25.5"),sQuery(id+"F0.wireOp",EDGE,"E25.6"),sQuery(id+"F0.wireOp",EDGE,"E25.7")])],"isStart":false})});var subQ1=sQuery(id+"F4.wireOp",EDGE,"E30");Q3=makeQuery(id+"F8.boolean.opBoolean","SPLIT",EDGE,{"disambiguationData":[TD([makeQuery(id+"F5.opExtrude","SWEPT_FACE",FACE,{"disambiguationData":[OSD([sQuery(id+"F4.wireOp",EDGE,"E35.filletArc")])]})])],"derivedFrom":makeQuery(id+"F5.opExtrude","TWEAK_EDGE",EDGE,{"derivedFrom":[subQ0,makeQuery(id+"F4.imprint","IMPRINT",EDGE,{"derivedFrom":subQ1})]})});}
            var Q4;
            {var subQ0=sQuery(id+"F0.wireOp",EDGE,"E25.0");var subQ1=sQuery(id+"F0.wireOp",EDGE,"E25.1");var subQ2=sQuery(id+"F0.wireOp",EDGE,"E25.2");var subQ3=sQuery(id+"F0.wireOp",EDGE,"E25.3");var subQ4=sQuery(id+"F0.wireOp",EDGE,"E25.4");var subQ5=sQuery(id+"F0.wireOp",EDGE,"E25.5");var subQ6=sQuery(id+"F0.wireOp",EDGE,"E25.6");var subQ7=sQuery(id+"F0.wireOp",EDGE,"E25.7");Q4=makeQuery(id+"F8.boolean.opBoolean","INTERSECT",EDGE,{"derivedFrom":[makeQuery(id+"F5.boolean.opBoolean","SPLIT",FACE,{"disambiguationData":[TD([makeQuery(id+"F2.opExtrude","SWEPT_FACE",FACE,{"disambiguationData":[OSD([subQ0])]})])],"derivedFrom":makeQuery(id+"F3.boolean.opBoolean","COPY",FACE,{"derivedFrom":makeQuery(id+"F3.opExtrude","CAP_FACE",FACE,{"disambiguationData":[OSD([subQ0,subQ1,subQ2,subQ3,subQ4,subQ5,subQ6,subQ7])],"isStart":false})})}),makeQuery(id+"F8.opExtrude","SWEPT_FACE",FACE,{"disambiguationData":[OSD([sQuery(id+"F7.wireOp",EDGE,"E67")])]})]});}
            var Q5;
            Q5=makeQuery(id+"F8.boolean.opBoolean","INTERSECT",EDGE,{"disambiguationData":[OD(0.0)],"derivedFrom":[makeQuery(id+"F5.opExtrude","SWEPT_FACE",FACE,{"disambiguationData":[OSD([sQuery(id+"F4.wireOp",EDGE,"E30")])]}),makeQuery(id+"F8.opExtrude","SWEPT_FACE",FACE,{"disambiguationData":[OSD([sQuery(id+"F7.wireOp",EDGE,"E67")])]})]});
            fillet(context, id + "F14", {"entities" : qUnion([Q0, Q1, Q2, Q3, Q4, Q5]), "radius" : 3 * mm, "tangentPropagation" : true, "allowEdgeOverflow" : false});
        }
        {
            var Q0;
            Q0=makeQuery(id+"F1.opExtrude","CAP_EDGE",EDGE,{"disambiguationData":[OSD([sQuery(id+"F0.wireOp",EDGE,"E1.bottom")])],"isStart":false});
            fillet(context, id + "F15", {"entities" : qUnion([Q0]), "radius" : 2 * mm, "tangentPropagation" : true, "allowEdgeOverflow" : false});
        }
        {
            var Q0;
            {var subQ0=sQuery(id+"F0.wireOp",EDGE,"E21.filletArc");var subQ1=sQuery(id+"F0.wireOp",EDGE,"E7");var subQ2=sQuery(id+"F0.wireOp",EDGE,"E6");var subQ3=sQuery(id+"F0.wireOp",EDGE,"E5");var subQ4=sQuery(id+"F0.wireOp",EDGE,"E4");var subQ5=sQuery(id+"F0.wireOp",EDGE,"E22.filletArc");var subQ6=sQuery(id+"F0.wireOp",EDGE,"E1.bottom");var subQ7=sQuery(id+"F0.wireOp",EDGE,"E1.right");var subQ8=sQuery(id+"F0.wireOp",EDGE,"E1.top");var subQ9=sQuery(id+"F0.wireOp",EDGE,"E1.left");var subQ10=sQuery(id+"F0.wireOp",EDGE,"E23.filletArc");var subQ11=sQuery(id+"F0.wireOp",EDGE,"E24.filletArc");Q0=makeQuery(id+"F2.boolean.opBoolean","SPLIT",FACE,{"disambiguationData":[TD([makeQuery(id+"F1.opExtrude","SWEPT_FACE",FACE,{"disambiguationData":[OSD([subQ6])]})])],"derivedFrom":makeQuery(id+"F1.opExtrude","CAP_FACE",FACE,{"disambiguationData":[OSD([subQ6,subQ8,subQ9,subQ7,subQ4,subQ3,subQ2,subQ1,subQ0,subQ5,subQ10,subQ11])],"isStart":true})});}
            var sketch = newSketch(context, id + "F16", { "sketchPlane" : qUnion([Q0])});
            skLineSegment(sketch, "E79.0.0", {"start": v(70, 90) * mm, "end": v(-70, 90) * mm});
            skArc(sketch, "E79.0.1", {"start": v(-70, 90) * mm, "mid": v(-77.07, 87.07) * mm, "end": v(-80, 80) * mm});
            skLineSegment(sketch, "E79.0.2", {"start": v(-80, 80) * mm, "end": v(-80, -80) * mm});
            skArc(sketch, "E79.0.3", {"start": v(-80, -80) * mm, "mid": v(-77.07, -87.07) * mm, "end": v(-70, -90) * mm});
            skLineSegment(sketch, "E79.0.4", {"start": v(-70, -90) * mm, "end": v(70, -90) * mm});
            skArc(sketch, "E79.0.5", {"start": v(70, -90) * mm, "mid": v(77.07, -87.07) * mm, "end": v(80, -80) * mm});
            skLineSegment(sketch, "E79.0.6", {"start": v(80, -80) * mm, "end": v(80, 80) * mm});
            skArc(sketch, "E79.0.7", {"start": v(80, 80) * mm, "mid": v(77.07, 87.07) * mm, "end": v(70, 90) * mm});
            skArc(sketch, "E80.0", {"start": v(56.15, 48.18) * mm, "mid": v(0, 67.5) * mm, "end": v(-56.15, 48.18) * mm});
            skLineSegment(sketch, "E80.1", {"start": v(-60, 40.3) * mm, "end": v(-60, -40.3) * mm});
            skArc(sketch, "E80.2", {"start": v(-56.15, 48.18) * mm, "mid": v(-58.99, 44.68) * mm, "end": v(-60, 40.3) * mm});
            skArc(sketch, "E80.3", {"start": v(60, 40.3) * mm, "mid": v(58.99, 44.68) * mm, "end": v(56.15, 48.18) * mm});
            skLineSegment(sketch, "E80.4", {"start": v(60, 40.3) * mm, "end": v(60, -40.3) * mm});
            skArc(sketch, "E80.5", {"start": v(56.15, -48.18) * mm, "mid": v(58.99, -44.68) * mm, "end": v(60, -40.3) * mm});
            skArc(sketch, "E80.6", {"start": v(-56.15, -48.18) * mm, "mid": v(0, -67.5) * mm, "end": v(56.15, -48.18) * mm});
            skArc(sketch, "E80.7", {"start": v(-60, -40.3) * mm, "mid": v(-58.99, -44.68) * mm, "end": v(-56.15, -48.18) * mm});
            skCircle(sketch, "E81.0", {"center": v(-60, 67.5) * mm, "radius": 4 * mm});
            skCircle(sketch, "E82.0", {"center": v(60, 67.5) * mm, "radius": 4 * mm});
            skCircle(sketch, "E82.1", {"center": v(60, -67.5) * mm, "radius": 4 * mm});
            skCircle(sketch, "E82.2", {"center": v(-60, -67.5) * mm, "radius": 4 * mm});
            skLineSegment(sketch, "E83", {"start": v(0, 90) * mm, "end": v(0, 120) * mm, "construction": true});
            skCircle(sketch, "E84", {"center": v(0, 120) * mm, "radius": 6 * mm});
            skLineSegment(sketch, "E85", {"start": v(33, 90) * mm, "end": v(15, 108) * mm});
            skLineSegment(sketch, "E86", {"start": v(-33, 90) * mm, "end": v(-15, 108) * mm});
            skLineSegment(sketch, "E87", {"start": v(-15, 108) * mm, "end": v(-15, 120) * mm});
            skLineSegment(sketch, "E88", {"start": v(15, 108) * mm, "end": v(15, 120) * mm});
            skArc(sketch, "E89", {"start": v(15, 120) * mm, "mid": v(0, 135) * mm, "end": v(-15, 120) * mm});
            skLineSegment(sketch, "E90", {"start": v(-80, 0) * mm, "end": v(80, 0) * mm, "construction": true});
            skLineSegment(sketch, "E91.MirrorCS", {"start": v(-33, -90) * mm, "end": v(-15, -108) * mm});
            skLineSegment(sketch, "E92.MirrorCS", {"start": v(-15, -108) * mm, "end": v(-15, -120) * mm});
            skArc(sketch, "E93.MirrorCS", {"start": v(15, -120) * mm, "mid": v(0, -135) * mm, "end": v(-15, -120) * mm});
            skLineSegment(sketch, "E94.MirrorCS", {"start": v(15, -108) * mm, "end": v(15, -120) * mm});
            skLineSegment(sketch, "E95.MirrorCS", {"start": v(33, -90) * mm, "end": v(15, -108) * mm});
            skCircle(sketch, "E96.MirrorC", {"center": v(0, -120) * mm, "radius": 6 * mm});
            skLineSegment(sketch, "E97.MirrorCS", {"start": v(0, -90) * mm, "end": v(0, -120) * mm, "construction": true});
            skSolve(sketch);
        }
        {
            var Q0;
            Q0 = qSketchRegion(id + "F16", true);
            var Q1;
            Q1=makeQuery(id+"F2.opExtrude","CAP_FACE",FACE,{"disambiguationData":[OSD([sQuery(id+"F0.wireOp",EDGE,"E12"),sQuery(id+"F0.wireOp",EDGE,"E13"),sQuery(id+"F0.wireOp",EDGE,"E14"),sQuery(id+"F0.wireOp",EDGE,"E15"),sQuery(id+"F0.wireOp",EDGE,"E17.filletArc"),sQuery(id+"F0.wireOp",EDGE,"E18.filletArc"),sQuery(id+"F0.wireOp",EDGE,"E19.filletArc"),sQuery(id+"F0.wireOp",EDGE,"E20.filletArc"),sQuery(id+"F0.wireOp",EDGE,"E25.0"),sQuery(id+"F0.wireOp",EDGE,"E25.1"),sQuery(id+"F0.wireOp",EDGE,"E25.2"),sQuery(id+"F0.wireOp",EDGE,"E25.3"),sQuery(id+"F0.wireOp",EDGE,"E25.4"),sQuery(id+"F0.wireOp",EDGE,"E25.5"),sQuery(id+"F0.wireOp",EDGE,"E25.6"),sQuery(id+"F0.wireOp",EDGE,"E25.7")])],"isStart":false});
            extrude(context, id + "F17", {"entities" : qUnion([Q0]), "endBound" : BoundingType.UP_TO_SURFACE, "depth" : 25 * mm, "endBoundEntityFace" : qUnion([Q1]), "offsetDistance" : 25 * mm});
        }
    });
